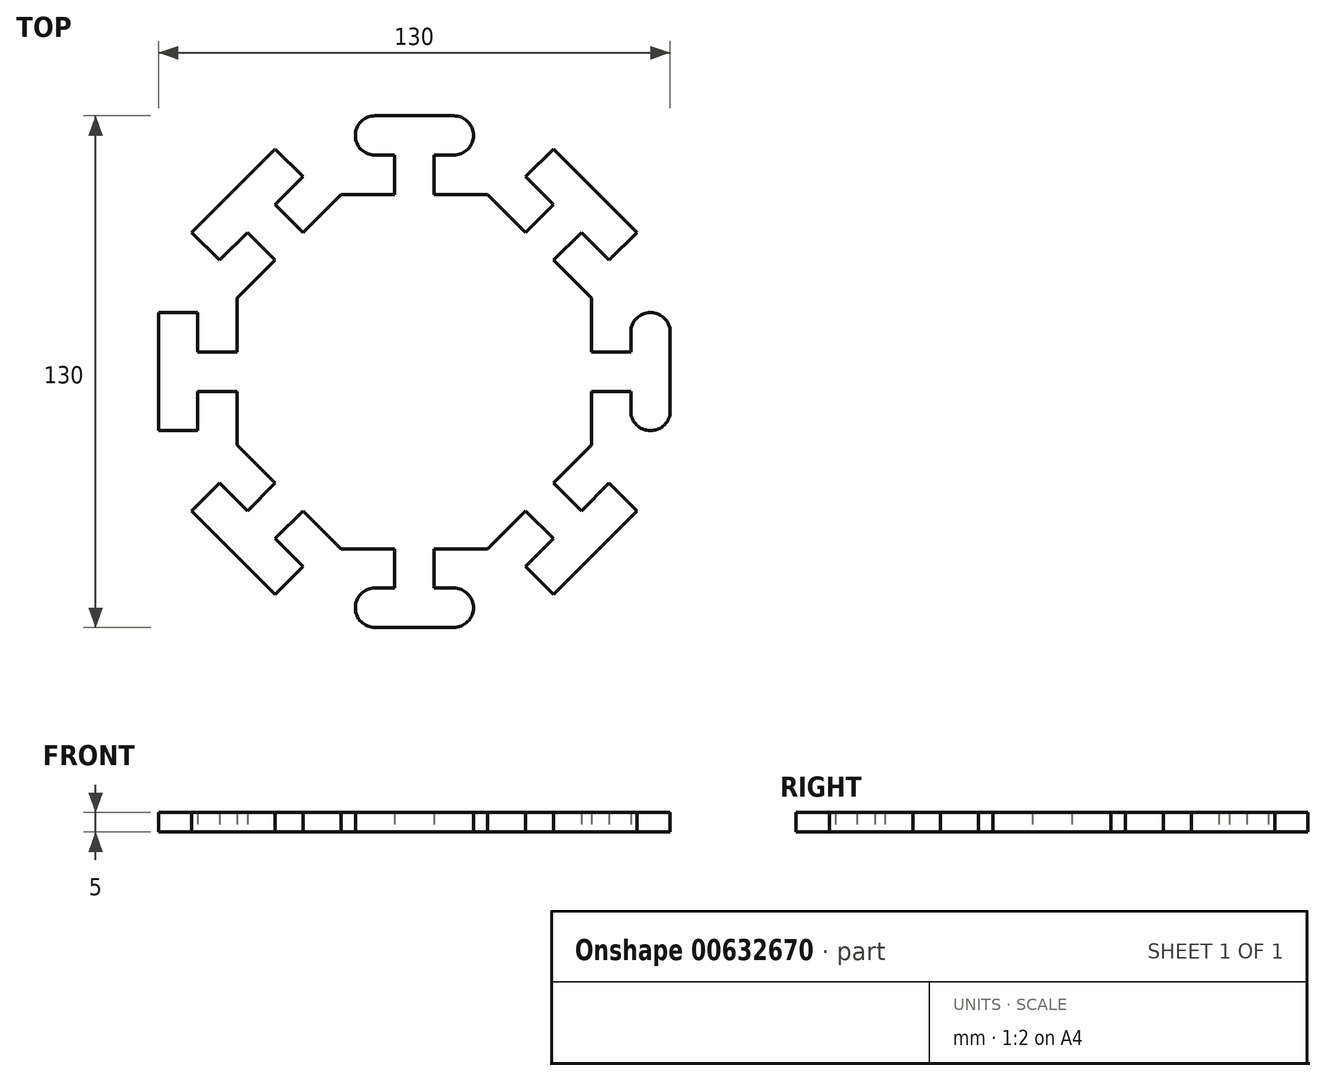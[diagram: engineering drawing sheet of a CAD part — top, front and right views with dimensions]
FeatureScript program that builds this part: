
annotation { "Feature Type Name" : "Feature", "Feature Type Description" : "" }
export const myFeature = defineFeature(function(context is Context, id is Id, definition is map)
    precondition{}
    {
        {
            var Q0;
            Q0=qCreatedBy(makeId("Top.planeOp"),FACE);
            var sketch = newSketch(context, id + "F0", { "sketchPlane" : qUnion([Q0])});
            skLineSegment(sketch, "E0.bottom", {"start": v(-15, 65) * mm, "end": v(15, 65) * mm});
            skLineSegment(sketch, "E0.top", {"start": v(-15, 55) * mm, "end": v(15, 55) * mm});
            skLineSegment(sketch, "E0.left", {"start": v(-15, 65) * mm, "end": v(-15, 55) * mm});
            skLineSegment(sketch, "E0.right", {"start": v(15, 65) * mm, "end": v(15, 55) * mm});
            skLineSegment(sketch, "E1.bottom", {"start": v(-5, -45) * mm, "end": v(5, -45) * mm});
            skLineSegment(sketch, "E1.top", {"start": v(-5, -55) * mm, "end": v(5, -55) * mm});
            skLineSegment(sketch, "E1.left", {"start": v(-5, -45) * mm, "end": v(-5, -55) * mm});
            skLineSegment(sketch, "E1.right", {"start": v(5, -45) * mm, "end": v(5, -55) * mm});
            skLineSegment(sketch, "E2.bottom", {"start": v(-15, -55) * mm, "end": v(15, -55) * mm});
            skLineSegment(sketch, "E2.top", {"start": v(-15, -65) * mm, "end": v(15, -65) * mm});
            skLineSegment(sketch, "E2.left", {"start": v(-15, -55) * mm, "end": v(-15, -65) * mm});
            skLineSegment(sketch, "E2.right", {"start": v(15, -55) * mm, "end": v(15, -65) * mm});
            skCircle(sketch, "E3.cCircle", {"center": v(0, 0) * mm, "radius": 45 * mm, "construction": true});
            skLineSegment(sketch, "E3.0", {"start": v(18.64, -45) * mm, "end": v(-18.64, -45) * mm});
            skLineSegment(sketch, "E3.1", {"start": v(-18.64, -45) * mm, "end": v(-45, -18.64) * mm});
            skLineSegment(sketch, "E3.2", {"start": v(-45, -18.64) * mm, "end": v(-45, 18.64) * mm});
            skLineSegment(sketch, "E3.3", {"start": v(-45, 18.64) * mm, "end": v(-18.64, 45) * mm});
            skLineSegment(sketch, "E3.4", {"start": v(-18.64, 45) * mm, "end": v(18.64, 45) * mm});
            skLineSegment(sketch, "E3.5", {"start": v(18.64, 45) * mm, "end": v(45, 18.64) * mm});
            skLineSegment(sketch, "E3.6", {"start": v(45, 18.64) * mm, "end": v(45, -18.64) * mm});
            skLineSegment(sketch, "E3.7", {"start": v(45, -18.64) * mm, "end": v(18.64, -45) * mm});
            skPoint(sketch, "E3.0.midPoint", {"position": v(0, -45) * mm});
            skLineSegment(sketch, "E4.bottom", {"start": v(-5, 55) * mm, "end": v(5, 55) * mm});
            skLineSegment(sketch, "E4.top", {"start": v(-5, 45) * mm, "end": v(5, 45) * mm});
            skLineSegment(sketch, "E4.left", {"start": v(-5, 55) * mm, "end": v(-5, 45) * mm});
            skLineSegment(sketch, "E4.right", {"start": v(5, 55) * mm, "end": v(5, 45) * mm});
            skLineSegment(sketch, "E5.bottom", {"start": v(55, 15) * mm, "end": v(65, 15) * mm});
            skLineSegment(sketch, "E5.top", {"start": v(55, -15) * mm, "end": v(65, -15) * mm});
            skLineSegment(sketch, "E5.left", {"start": v(55, 15) * mm, "end": v(55, -15) * mm});
            skLineSegment(sketch, "E5.right", {"start": v(65, 15) * mm, "end": v(65, -15) * mm});
            skLineSegment(sketch, "E6.bottom", {"start": v(45, 5) * mm, "end": v(55, 5) * mm});
            skLineSegment(sketch, "E6.top", {"start": v(45, -5) * mm, "end": v(55, -5) * mm});
            skLineSegment(sketch, "E6.left", {"start": v(45, 5) * mm, "end": v(45, -5) * mm});
            skLineSegment(sketch, "E6.right", {"start": v(55, 5) * mm, "end": v(55, -5) * mm});
            skLineSegment(sketch, "E7.MirrorCS", {"start": v(5, -55) * mm, "end": v(-5, -55) * mm});
            skLineSegment(sketch, "E8.MirrorCS", {"start": v(5, 55) * mm, "end": v(-5, 55) * mm});
            skLineSegment(sketch, "E9.MirrorCS", {"start": v(5, 45) * mm, "end": v(-5, 45) * mm});
            skLineSegment(sketch, "E10.MirrorCS", {"start": v(5, -45) * mm, "end": v(-5, -45) * mm});
            skLineSegment(sketch, "E11.MirrorCS", {"start": v(45, 18.64) * mm, "end": v(18.64, 45) * mm});
            skLineSegment(sketch, "E12.MirrorCS", {"start": v(18.64, -45) * mm, "end": v(45, -18.64) * mm});
            skLineSegment(sketch, "E13.MirrorCS", {"start": v(15, 65) * mm, "end": v(-15, 65) * mm});
            skLineSegment(sketch, "E14.MirrorCS", {"start": v(15, 55) * mm, "end": v(-15, 55) * mm});
            skLineSegment(sketch, "E15.MirrorCS", {"start": v(-18.64, 45) * mm, "end": v(-45, 18.64) * mm});
            skLineSegment(sketch, "E16.MirrorCS", {"start": v(-18.64, -45) * mm, "end": v(18.64, -45) * mm});
            skLineSegment(sketch, "E17.MirrorCS", {"start": v(-45, 18.64) * mm, "end": v(-45, -18.64) * mm});
            skLineSegment(sketch, "E18.MirrorCS", {"start": v(45, -18.64) * mm, "end": v(45, 18.64) * mm});
            skLineSegment(sketch, "E19.MirrorCS", {"start": v(18.64, 45) * mm, "end": v(-18.64, 45) * mm});
            skLineSegment(sketch, "E20.MirrorCS", {"start": v(15, -55) * mm, "end": v(-15, -55) * mm});
            skLineSegment(sketch, "E21.MirrorCS", {"start": v(15, -65) * mm, "end": v(-15, -65) * mm});
            skLineSegment(sketch, "E22.MirrorCS", {"start": v(-45, -18.64) * mm, "end": v(-18.64, -45) * mm});
            skPoint(sketch, "E23.center", {"position": v(-0.34, 0.14) * mm});
            skLineSegment(sketch, "E24.MirrorCS", {"start": v(-45, 5) * mm, "end": v(-45, -5) * mm});
            skLineSegment(sketch, "E25.MirrorCS", {"start": v(-55, 5) * mm, "end": v(-55, -5) * mm});
            skLineSegment(sketch, "E26.MirrorCS", {"start": v(-45, 5) * mm, "end": v(-55, 5) * mm});
            skLineSegment(sketch, "E27.MirrorCS", {"start": v(-55, 15) * mm, "end": v(-65, 15) * mm});
            skLineSegment(sketch, "E28.MirrorCS", {"start": v(-45, -5) * mm, "end": v(-55, -5) * mm});
            skPoint(sketch, "E29.MirrorP", {"position": v(0.34, 0.14) * mm});
            skLineSegment(sketch, "E30.MirrorCS", {"start": v(-55, -15) * mm, "end": v(-65, -15) * mm});
            skLineSegment(sketch, "E31.MirrorCS", {"start": v(-65, 15) * mm, "end": v(-65, -15) * mm});
            skLineSegment(sketch, "E32.MirrorCS", {"start": v(-55, 15) * mm, "end": v(-55, -15) * mm});
            skLineSegment(sketch, "E33", {"start": v(-18.64, 45) * mm, "end": v(18.64, -45) * mm});
            skLineSegment(sketch, "E34.MirrorCS", {"start": v(28.28, -35.36) * mm, "end": v(35.36, -42.43) * mm});
            skLineSegment(sketch, "E35.MirrorCS", {"start": v(28.28, -35.36) * mm, "end": v(35.36, -28.28) * mm});
            skLineSegment(sketch, "E36.MirrorCS", {"start": v(-35.36, 28.28) * mm, "end": v(-28.28, 35.36) * mm});
            skLineSegment(sketch, "E37.MirrorCS", {"start": v(-28.28, 35.36) * mm, "end": v(-35.36, 28.28) * mm});
            skLineSegment(sketch, "E38.MirrorCS", {"start": v(35.36, -28.28) * mm, "end": v(28.28, -35.36) * mm});
            skLineSegment(sketch, "E39.MirrorCS", {"start": v(-35.36, 42.43) * mm, "end": v(-42.43, 35.36) * mm});
            skLineSegment(sketch, "E40.MirrorCS", {"start": v(-42.43, 35.36) * mm, "end": v(-35.36, 42.43) * mm});
            skLineSegment(sketch, "E41.MirrorCS", {"start": v(35.36, -28.28) * mm, "end": v(42.43, -35.36) * mm});
            skLineSegment(sketch, "E42.MirrorCS", {"start": v(35.36, -42.43) * mm, "end": v(42.43, -35.36) * mm});
            skLineSegment(sketch, "E43.MirrorCS", {"start": v(42.43, -35.36) * mm, "end": v(35.36, -42.43) * mm});
            skLineSegment(sketch, "E44.MirrorCS", {"start": v(49.5, -28.28) * mm, "end": v(56.57, -35.36) * mm});
            skPoint(sketch, "E45.MirrorP", {"position": v(31.82, -31.82) * mm});
            skLineSegment(sketch, "E46.MirrorCS", {"start": v(35.36, -56.57) * mm, "end": v(56.57, -35.36) * mm});
            skLineSegment(sketch, "E47.MirrorCS", {"start": v(-35.36, 56.57) * mm, "end": v(-28.28, 49.5) * mm});
            skLineSegment(sketch, "E48.MirrorCS", {"start": v(28.28, -49.5) * mm, "end": v(35.36, -56.57) * mm});
            skLineSegment(sketch, "E49.MirrorCS", {"start": v(-35.36, 42.43) * mm, "end": v(-28.28, 35.36) * mm});
            skLineSegment(sketch, "E50.MirrorCS", {"start": v(-56.57, 35.36) * mm, "end": v(-35.36, 56.57) * mm});
            skLineSegment(sketch, "E51.MirrorCS", {"start": v(-28.28, 49.5) * mm, "end": v(-49.5, 28.28) * mm});
            skLineSegment(sketch, "E52.MirrorCS", {"start": v(28.28, -49.5) * mm, "end": v(49.5, -28.28) * mm});
            skLineSegment(sketch, "E53.MirrorCS", {"start": v(-42.43, 35.36) * mm, "end": v(-35.36, 28.28) * mm});
            skLineSegment(sketch, "E54.MirrorCS", {"start": v(-56.57, 35.36) * mm, "end": v(-49.5, 28.28) * mm});
            skLineSegment(sketch, "E55.MirrorCS", {"start": v(-35.36, -28.28) * mm, "end": v(-28.28, -35.36) * mm});
            skLineSegment(sketch, "E56.MirrorCS", {"start": v(28.28, 35.36) * mm, "end": v(35.36, 28.28) * mm});
            skLineSegment(sketch, "E57.MirrorCS", {"start": v(-49.5, 28.28) * mm, "end": v(-28.28, 49.5) * mm});
            skLineSegment(sketch, "E58.MirrorCS", {"start": v(-28.28, -35.36) * mm, "end": v(-35.36, -42.43) * mm});
            skLineSegment(sketch, "E59.MirrorCS", {"start": v(-35.36, 56.57) * mm, "end": v(-56.57, 35.36) * mm});
            skLineSegment(sketch, "E60.MirrorCS", {"start": v(-42.43, -35.36) * mm, "end": v(-35.36, -42.43) * mm});
            skLineSegment(sketch, "E61.MirrorCS", {"start": v(49.5, -28.28) * mm, "end": v(28.28, -49.5) * mm});
            skLineSegment(sketch, "E62.MirrorCS", {"start": v(56.57, -35.36) * mm, "end": v(35.36, -56.57) * mm});
            skLineSegment(sketch, "E63.MirrorCS", {"start": v(-49.5, -28.28) * mm, "end": v(-56.57, -35.36) * mm});
            skPoint(sketch, "E64.MirrorP", {"position": v(0.14, 0.34) * mm});
            skLineSegment(sketch, "E65.MirrorCS", {"start": v(35.36, 42.43) * mm, "end": v(42.43, 35.36) * mm});
            skLineSegment(sketch, "E66.MirrorCS", {"start": v(35.36, 56.57) * mm, "end": v(56.57, 35.36) * mm});
            skLineSegment(sketch, "E67.MirrorCS", {"start": v(28.28, 49.5) * mm, "end": v(49.5, 28.28) * mm});
            skLineSegment(sketch, "E68.MirrorCS", {"start": v(-49.5, -28.28) * mm, "end": v(-28.28, -49.5) * mm});
            skLineSegment(sketch, "E69.MirrorCS", {"start": v(-35.36, -28.28) * mm, "end": v(-42.43, -35.36) * mm});
            skLineSegment(sketch, "E70.MirrorCS", {"start": v(28.28, 49.5) * mm, "end": v(35.36, 56.57) * mm});
            skLineSegment(sketch, "E71.MirrorCS", {"start": v(-56.57, -35.36) * mm, "end": v(-35.36, -56.57) * mm});
            skPoint(sketch, "E72.MirrorP", {"position": v(-0.34, -0.14) * mm});
            skLineSegment(sketch, "E73.MirrorCS", {"start": v(35.36, 28.28) * mm, "end": v(42.43, 35.36) * mm});
            skLineSegment(sketch, "E74.MirrorCS", {"start": v(49.5, 28.28) * mm, "end": v(56.57, 35.36) * mm});
            skLineSegment(sketch, "E75.MirrorCS", {"start": v(28.28, 35.36) * mm, "end": v(35.36, 42.43) * mm});
            skLineSegment(sketch, "E76.MirrorCS", {"start": v(-28.28, -49.5) * mm, "end": v(-35.36, -56.57) * mm});
            skSolve(sketch);
        }
        {
            var Q0;
            Q0 = qSketchRegion(id + "F0", true);
            extrude(context, id + "F1", {"entities" : qUnion([Q0]), "depth" : 5 * mm, "offsetDistance" : 25 * mm});
        }
        {
            var Q0;
            Q0=makeQuery(id+"F1.opExtrude","SWEPT_EDGE",EDGE,{"disambiguationData":[OSD([sQuery(id+"F0.wireOp",EDGE,"E23.7.5"),sQuery(id+"F0.wireOp",EDGE,"E23.7.6")])]});
            var Q1;
            Q1=makeQuery(id+"F1.opExtrude","SWEPT_EDGE",EDGE,{"disambiguationData":[OSD([sQuery(id+"F0.wireOp",EDGE,"E23.7.4"),sQuery(id+"F0.wireOp",EDGE,"E23.7.5")])]});
            var Q2;
            Q2=makeQuery(id+"F1.opExtrude","SWEPT_EDGE",EDGE,{"disambiguationData":[OSD([sQuery(id+"F0.wireOp",EDGE,"E13.MirrorCS"),sQuery(id+"F0.wireOp",EDGE,"E0.right")])]});
            var Q3;
            Q3=makeQuery(id+"F1.opExtrude","SWEPT_EDGE",EDGE,{"disambiguationData":[OSD([sQuery(id+"F0.wireOp",EDGE,"E14.MirrorCS"),sQuery(id+"F0.wireOp",EDGE,"E0.right")])]});
            var Q4;
            Q4=makeQuery(id+"F1.opExtrude","SWEPT_EDGE",EDGE,{"disambiguationData":[OSD([sQuery(id+"F0.wireOp",EDGE,"E23.7.6"),sQuery(id+"F0.wireOp",EDGE,"E23.7.9")])]});
            var Q5;
            Q5=makeQuery(id+"F1.opExtrude","SWEPT_EDGE",EDGE,{"disambiguationData":[OSD([sQuery(id+"F0.wireOp",EDGE,"E5.bottom"),sQuery(id+"F0.wireOp",EDGE,"E5.right")])]});
            var Q6;
            Q6=makeQuery(id+"F1.opExtrude","SWEPT_EDGE",EDGE,{"disambiguationData":[OSD([sQuery(id+"F0.wireOp",EDGE,"E5.top"),sQuery(id+"F0.wireOp",EDGE,"E5.right")])]});
            var Q7;
            Q7=makeQuery(id+"F1.opExtrude","SWEPT_EDGE",EDGE,{"disambiguationData":[OSD([sQuery(id+"F0.wireOp",EDGE,"E23.5.4"),sQuery(id+"F0.wireOp",EDGE,"E23.5.5")])]});
            var Q8;
            Q8=makeQuery(id+"F1.opExtrude","SWEPT_EDGE",EDGE,{"disambiguationData":[OSD([sQuery(id+"F0.wireOp",EDGE,"E23.5.4"),sQuery(id+"F0.wireOp",EDGE,"E23.5.9")])]});
            var Q9;
            Q9=makeQuery(id+"F1.opExtrude","SWEPT_EDGE",EDGE,{"disambiguationData":[OSD([sQuery(id+"F0.wireOp",EDGE,"E2.right"),sQuery(id+"F0.wireOp",EDGE,"E21.MirrorCS")])]});
            var Q10;
            Q10=makeQuery(id+"F1.opExtrude","SWEPT_EDGE",EDGE,{"disambiguationData":[OSD([sQuery(id+"F0.wireOp",EDGE,"E2.right"),sQuery(id+"F0.wireOp",EDGE,"E20.MirrorCS")])]});
            var Q11;
            Q11=makeQuery(id+"F1.opExtrude","SWEPT_EDGE",EDGE,{"disambiguationData":[OSD([sQuery(id+"F0.wireOp",EDGE,"E23.3.4"),sQuery(id+"F0.wireOp",EDGE,"E23.3.9")])]});
            var Q12;
            Q12=makeQuery(id+"F1.opExtrude","SWEPT_EDGE",EDGE,{"disambiguationData":[OSD([sQuery(id+"F0.wireOp",EDGE,"E23.3.4"),sQuery(id+"F0.wireOp",EDGE,"E23.3.5")])]});
            var Q13;
            Q13=makeQuery(id+"F1.opExtrude","SWEPT_EDGE",EDGE,{"disambiguationData":[OSD([sQuery(id+"F0.wireOp",EDGE,"E23.3.6"),sQuery(id+"F0.wireOp",EDGE,"E23.3.9")])]});
            var Q14;
            Q14=makeQuery(id+"F1.opExtrude","SWEPT_EDGE",EDGE,{"disambiguationData":[OSD([sQuery(id+"F0.wireOp",EDGE,"E83.MirrorCS"),sQuery(id+"F0.wireOp",EDGE,"f1c53b1c-3f52-402c-a672-c7c4c914dd5020.MirrorCS")])]});
            var Q15;
            Q15=makeQuery(id+"F1.opExtrude","SWEPT_EDGE",EDGE,{"disambiguationData":[OSD([sQuery(id+"F0.wireOp",EDGE,"E2.left"),sQuery(id+"F0.wireOp",EDGE,"E21.MirrorCS")])]});
            var Q16;
            Q16=makeQuery(id+"F1.opExtrude","SWEPT_EDGE",EDGE,{"disambiguationData":[OSD([sQuery(id+"F0.wireOp",EDGE,"E23.3.5"),sQuery(id+"F0.wireOp",EDGE,"E23.3.6")])]});
            var Q17;
            Q17=makeQuery(id+"F1.opExtrude","SWEPT_EDGE",EDGE,{"disambiguationData":[OSD([sQuery(id+"F0.wireOp",EDGE,"f1c53b1c-3f52-402c-a672-c7c4c914dd508.MirrorCS"),sQuery(id+"F0.wireOp",EDGE,"f1c53b1c-3f52-402c-a672-c7c4c914dd5020.MirrorCS")])]});
            var Q18;
            Q18=makeQuery(id+"F1.opExtrude","SWEPT_EDGE",EDGE,{"disambiguationData":[OSD([sQuery(id+"F0.wireOp",EDGE,"f1c53b1c-3f52-402c-a672-c7c4c914dd502.MirrorCS"),sQuery(id+"F0.wireOp",EDGE,"E83.MirrorCS")])]});
            var Q19;
            Q19=makeQuery(id+"F1.opExtrude","SWEPT_EDGE",EDGE,{"disambiguationData":[OSD([sQuery(id+"F0.wireOp",EDGE,"E23.1.4"),sQuery(id+"F0.wireOp",EDGE,"E23.1.9")])]});
            var Q20;
            Q20=makeQuery(id+"F1.opExtrude","SWEPT_EDGE",EDGE,{"disambiguationData":[OSD([sQuery(id+"F0.wireOp",EDGE,"E23.1.4"),sQuery(id+"F0.wireOp",EDGE,"E23.1.5")])]});
            var Q21;
            Q21=makeQuery(id+"F1.opExtrude","SWEPT_EDGE",EDGE,{"disambiguationData":[OSD([sQuery(id+"F0.wireOp",EDGE,"E23.5.5"),sQuery(id+"F0.wireOp",EDGE,"E23.5.6")])]});
            var Q22;
            Q22=makeQuery(id+"F1.opExtrude","SWEPT_EDGE",EDGE,{"disambiguationData":[OSD([sQuery(id+"F0.wireOp",EDGE,"E23.5.6"),sQuery(id+"F0.wireOp",EDGE,"E23.5.9")])]});
            var Q23;
            Q23=makeQuery(id+"F1.opExtrude","SWEPT_EDGE",EDGE,{"disambiguationData":[OSD([sQuery(id+"F0.wireOp",EDGE,"f1c53b1c-3f52-402c-a672-c7c4c914dd502.MirrorCS"),sQuery(id+"F0.wireOp",EDGE,"f1c53b1c-3f52-402c-a672-c7c4c914dd508.MirrorCS")])]});
            var Q24;
            Q24=makeQuery(id+"F1.opExtrude","SWEPT_EDGE",EDGE,{"disambiguationData":[OSD([sQuery(id+"F0.wireOp",EDGE,"E23.7.4"),sQuery(id+"F0.wireOp",EDGE,"E23.7.9")])]});
            var Q25;
            Q25=makeQuery(id+"F1.opExtrude","SWEPT_EDGE",EDGE,{"disambiguationData":[OSD([sQuery(id+"F0.wireOp",EDGE,"E14.MirrorCS"),sQuery(id+"F0.wireOp",EDGE,"E0.left")])]});
            var Q26;
            Q26=makeQuery(id+"F1.opExtrude","SWEPT_EDGE",EDGE,{"disambiguationData":[OSD([sQuery(id+"F0.wireOp",EDGE,"E23.1.6"),sQuery(id+"F0.wireOp",EDGE,"E23.1.9")])]});
            var Q27;
            Q27=makeQuery(id+"F1.opExtrude","SWEPT_EDGE",EDGE,{"disambiguationData":[OSD([sQuery(id+"F0.wireOp",EDGE,"E13.MirrorCS"),sQuery(id+"F0.wireOp",EDGE,"E0.left")])]});
            var Q28;
            Q28=makeQuery(id+"F1.opExtrude","SWEPT_EDGE",EDGE,{"disambiguationData":[OSD([sQuery(id+"F0.wireOp",EDGE,"E23.1.5"),sQuery(id+"F0.wireOp",EDGE,"E23.1.6")])]});
            var Q29;
            Q29=makeQuery(id+"F1.opExtrude","SWEPT_EDGE",EDGE,{"disambiguationData":[OSD([sQuery(id+"F0.wireOp",EDGE,"E2.left"),sQuery(id+"F0.wireOp",EDGE,"E20.MirrorCS")])]});
            var Q30;
            Q30=makeQuery(id+"F1.opExtrude","SWEPT_EDGE",EDGE,{"disambiguationData":[OSD([sQuery(id+"F0.wireOp",EDGE,"E5.bottom"),sQuery(id+"F0.wireOp",EDGE,"E5.left")])]});
            var Q31;
            Q31=makeQuery(id+"F1.opExtrude","SWEPT_EDGE",EDGE,{"disambiguationData":[OSD([sQuery(id+"F0.wireOp",EDGE,"E5.top"),sQuery(id+"F0.wireOp",EDGE,"E5.left")])]});
            fillet(context, id + "F2", {"entities" : qUnion([Q0, Q1, Q2, Q3, Q4, Q5, Q6, Q7, Q8, Q9, Q10, Q11, Q12, Q13, Q14, Q15, Q16, Q17, Q18, Q19, Q20, Q21, Q22, Q23, Q24, Q25, Q26, Q27, Q28, Q29, Q30, Q31]), "radius" : 5 * mm, "tangentPropagation" : true, "allowEdgeOverflow" : false});
        }
    });
